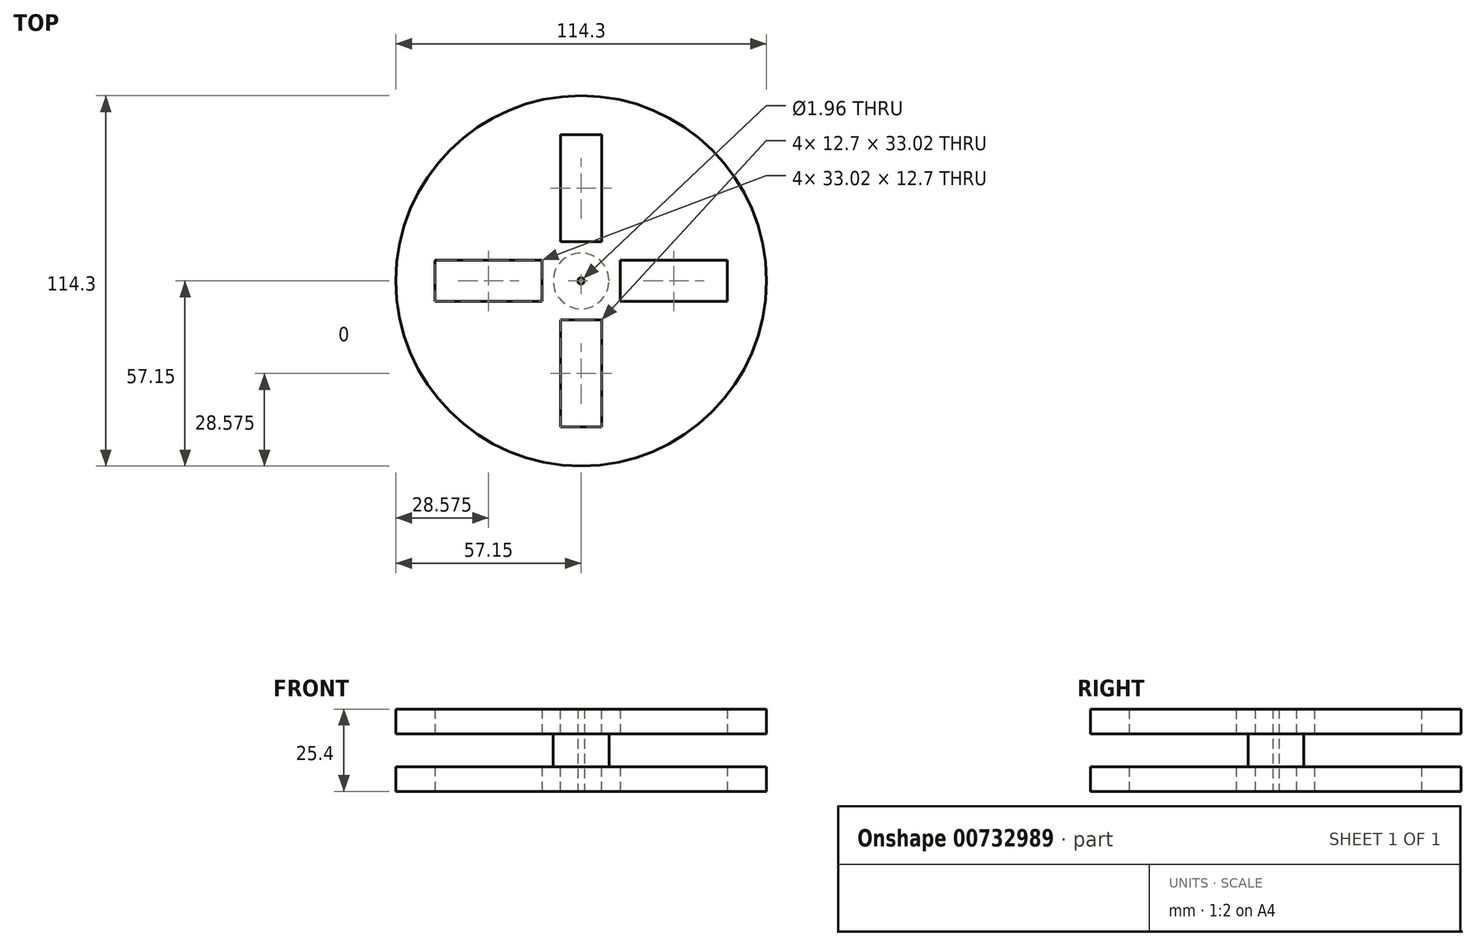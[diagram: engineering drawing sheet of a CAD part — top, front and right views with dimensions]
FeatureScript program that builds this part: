
annotation { "Feature Type Name" : "Feature", "Feature Type Description" : "" }
export const myFeature = defineFeature(function(context is Context, id is Id, definition is map)
    precondition{}
    {
        {
            var Q0;
            Q0=qCreatedBy(makeId("Top.planeOp"),FACE);
            var sketch = newSketch(context, id + "F0", { "sketchPlane" : qUnion([Q0])});
            skCircle(sketch, "E0", {"center": v(0, 0) * mm, "radius": 0.98 * mm});
            skCircle(sketch, "E1", {"center": v(0, 0) * mm, "radius": 57.15 * mm});
            skSolve(sketch);
        }
        {
            var Q0;
            Q0 = qSketchRegion(id + "F0", true);
            extrude(context, id + "F1", {"entities" : qUnion([Q0]), "depth" : 25.4 * mm, "offsetDistance" : 25.4 * mm});
        }
        {
            var Q0;
            Q0=makeQuery(id+"F1.opExtrude","SWEPT_FACE",FACE,{"disambiguationData":[OSD([sQuery(id+"F0.wireOp",EDGE,"E1")])]});
            shell(context, id + "F2", {"entities" : qUnion([Q0]), "thickness" : 12.7 * mm});
        }
        {
            var Q0;
            Q0=makeQuery(id+"F1.opExtrude","SWEPT_FACE",FACE,{"disambiguationData":[OSD([sQuery(id+"F0.wireOp",EDGE,"E1")])]});
            shell(context, id + "F3", {"entities" : qUnion([Q0]), "thickness" : 7.62 * mm});
        }
        {
            var Q0;
            Q0=makeQuery(id+"F1.opExtrude","CAP_FACE",FACE,{"disambiguationData":[OSD([sQuery(id+"F0.wireOp",EDGE,"E0"),sQuery(id+"F0.wireOp",EDGE,"E1")])],"isStart":false});
            var sketch = newSketch(context, id + "F4", { "sketchPlane" : qUnion([Q0])});
            skLineSegment(sketch, "E2.bottom", {"start": v(6.35, 12.07) * mm, "end": v(-6.35, 12.07) * mm});
            skLineSegment(sketch, "E2.top", {"start": v(6.35, 45.09) * mm, "end": v(-6.35, 45.09) * mm});
            skLineSegment(sketch, "E2.left", {"start": v(6.35, 12.07) * mm, "end": v(6.35, 45.09) * mm});
            skLineSegment(sketch, "E2.right", {"start": v(-6.35, 12.07) * mm, "end": v(-6.35, 45.09) * mm});
            skPoint(sketch, "E2.middle", {"position": v(0, 28.58) * mm});
            skLineSegment(sketch, "E3", {"start": v(-57.15, 0) * mm, "end": v(57.15, 0) * mm});
            skLineSegment(sketch, "E4.MirrorCS", {"start": v(6.35, -12.07) * mm, "end": v(6.35, -45.09) * mm});
            skLineSegment(sketch, "E5.MirrorCS", {"start": v(6.35, -45.09) * mm, "end": v(-6.35, -45.09) * mm});
            skLineSegment(sketch, "E6.MirrorCS", {"start": v(-6.35, -12.07) * mm, "end": v(-6.35, -45.09) * mm});
            skLineSegment(sketch, "E7.MirrorCS", {"start": v(6.35, -12.07) * mm, "end": v(-6.35, -12.07) * mm});
            skLineSegment(sketch, "E8", {"start": v(0.98, 0) * mm, "end": v(57.15, 0) * mm});
            skPoint(sketch, "E9", {"position": v(29.06, 0) * mm});
            skPoint(sketch, "E10.endSnap0", {"position": v(0, 45.09) * mm});
            skPoint(sketch, "E11", {"position": v(14.53, 14.29) * mm});
            skPoint(sketch, "E12.middle", {"position": v(25.37, 24.8) * mm});
            skPoint(sketch, "E13", {"position": v(25.37, 8.3) * mm});
            skSolve(sketch);
        }
        {
            var Q0;
            Q0=makeQuery(id+"F4.imprint","IMPRINT",FACE,{"disambiguationData":[TD([[makeQuery(id+"F4.imprint","IMPRINT",EDGE,{"derivedFrom":sQuery(id+"F4.wireOp",EDGE,"E4.MirrorCS")}),-1.0]])]});
            extrude(context, id + "F5", {"entities" : qUnion([Q0]), "operationType" : NewBodyOperationType.REMOVE, "oppositeDirection" : true, "depth" : 25.4 * mm, "offsetDistance" : 25.4 * mm});
        }
        {
            var Q0;
            Q0 = qSketchRegion(id + "F4", true);
            extrude(context, id + "F6", {"entities" : qUnion([Q0]), "operationType" : NewBodyOperationType.REMOVE, "oppositeDirection" : true, "depth" : 25.4 * mm, "offsetDistance" : 25.4 * mm});
        }
        {
            var Q0;
            Q0=makeQuery(id+"F1.opExtrude","CAP_FACE",FACE,{"disambiguationData":[OSD([sQuery(id+"F0.wireOp",EDGE,"E0"),sQuery(id+"F0.wireOp",EDGE,"E1")])],"isStart":true});
            var sketch = newSketch(context, id + "F7", { "sketchPlane" : qUnion([Q0])});
            skLineSegment(sketch, "E14", {"start": v(0, 0) * mm, "end": v(57.15, 0) * mm});
            skLineSegment(sketch, "E15", {"start": v(57.15, 0) * mm, "end": v(-57.15, 0) * mm});
            skLineSegment(sketch, "E16.bottom", {"start": v(12.07, -6.35) * mm, "end": v(45.09, -6.35) * mm});
            skLineSegment(sketch, "E16.top", {"start": v(12.06, 6.35) * mm, "end": v(45.09, 6.35) * mm});
            skLineSegment(sketch, "E16.left", {"start": v(12.07, -6.35) * mm, "end": v(12.06, 6.35) * mm});
            skLineSegment(sketch, "E16.right", {"start": v(45.09, -6.35) * mm, "end": v(45.09, 6.35) * mm});
            skPoint(sketch, "E16.middle", {"position": v(28.58, 0) * mm});
            skLineSegment(sketch, "E17", {"start": v(6.35, -12.07) * mm, "end": v(6.35, -45.09) * mm});
            skLineSegment(sketch, "E18", {"start": v(6.35, -12.07) * mm, "end": v(-6.35, -12.07) * mm});
            skLineSegment(sketch, "E19", {"start": v(0, 12.07) * mm, "end": v(0, 0) * mm});
            skLineSegment(sketch, "E20", {"start": v(0, 0) * mm, "end": v(12.07, 0) * mm});
            skLineSegment(sketch, "E21", {"start": v(12.07, 0) * mm, "end": v(0, 0) * mm});
            skLineSegment(sketch, "E22", {"start": v(0, -12.07) * mm, "end": v(0, 0) * mm});
            skLineSegment(sketch, "E23", {"start": v(0, -12.07) * mm, "end": v(0, 12.07) * mm});
            skLineSegment(sketch, "E24.MirrorCS", {"start": v(-12.07, -6.35) * mm, "end": v(-12.06, 6.35) * mm});
            skLineSegment(sketch, "E25.MirrorCS", {"start": v(-12.06, -6.35) * mm, "end": v(-45.09, -6.35) * mm});
            skLineSegment(sketch, "E26.MirrorCS", {"start": v(-12.06, 6.35) * mm, "end": v(-45.09, 6.35) * mm});
            skLineSegment(sketch, "E27.MirrorCS", {"start": v(-45.09, -6.35) * mm, "end": v(-45.09, 6.35) * mm});
            skSolve(sketch);
        }
        {
            var Q0;
            Q0 = qSketchRegion(id + "F7", true);
            extrude(context, id + "F8", {"entities" : qUnion([Q0]), "operationType" : NewBodyOperationType.REMOVE, "oppositeDirection" : true, "depth" : 25.4 * mm, "offsetDistance" : 25.4 * mm});
        }
    });
